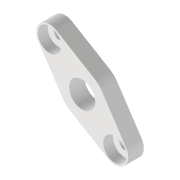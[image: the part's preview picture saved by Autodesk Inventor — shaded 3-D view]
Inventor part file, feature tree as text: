
AUTODESK INVENTOR PART (.ipt)
format: ipt  version: 2022 (Build 260153000, 153)  size: 137,728 bytes
history: native  units: mm
features: reference x6, sketch x4, extrude x3, other x2, hole x1, projected_geometry x1
ambient origin geometry x8: Origin, YZ Plane, XZ Plane, XY Plane, X Axis, Y Axis, Z Axis, Center Point
bodies: Volumenkörper1 (feature_tree)
feature tree (17):
  extrude  "Extrusion1"  Depth=4.0mm
  extrude  "Extrusion2"  Depth=3.0mm
  extrude  "Extrusion3"  [1 undecoded]
  hole  "Bohrung1"  [1 undecoded]
  sketch  "Skizze1"  dims[d0=4.0mm d1=0.0mm d2=2.0mm]
  reference  "Referenz1"
  reference  "Referenz2"
  reference  "Referenz3"
  sketch  "Skizze2"  dims[d3=3.0mm d4=0.0mm d5=6.7mm]
  projected_geometry  "Projizierte Kontur1"
  sketch  "Skizze3"  dims[d6=3.0mm d7=0.0mm]
  reference  "Referenz4"
  reference  "Referenz5"
  reference  "Referenz6"
  sketch  "Skizze4"  dims[d8=2.8mm d9=6.0mm d10=6.0mm d11=2.5mm d12=90.0deg d13=8.0mm d14=20.594885mm]
  other  "Assembly_Matchboxscope_injectionmolded.iam"
  other  "IM_Matchboxscope_base:1"
note: 2 required parameter values undecoded (feature->parameter linkage not recoverable at this tier; creation-order binding heuristic only, values carry confidence <= 0.55)
